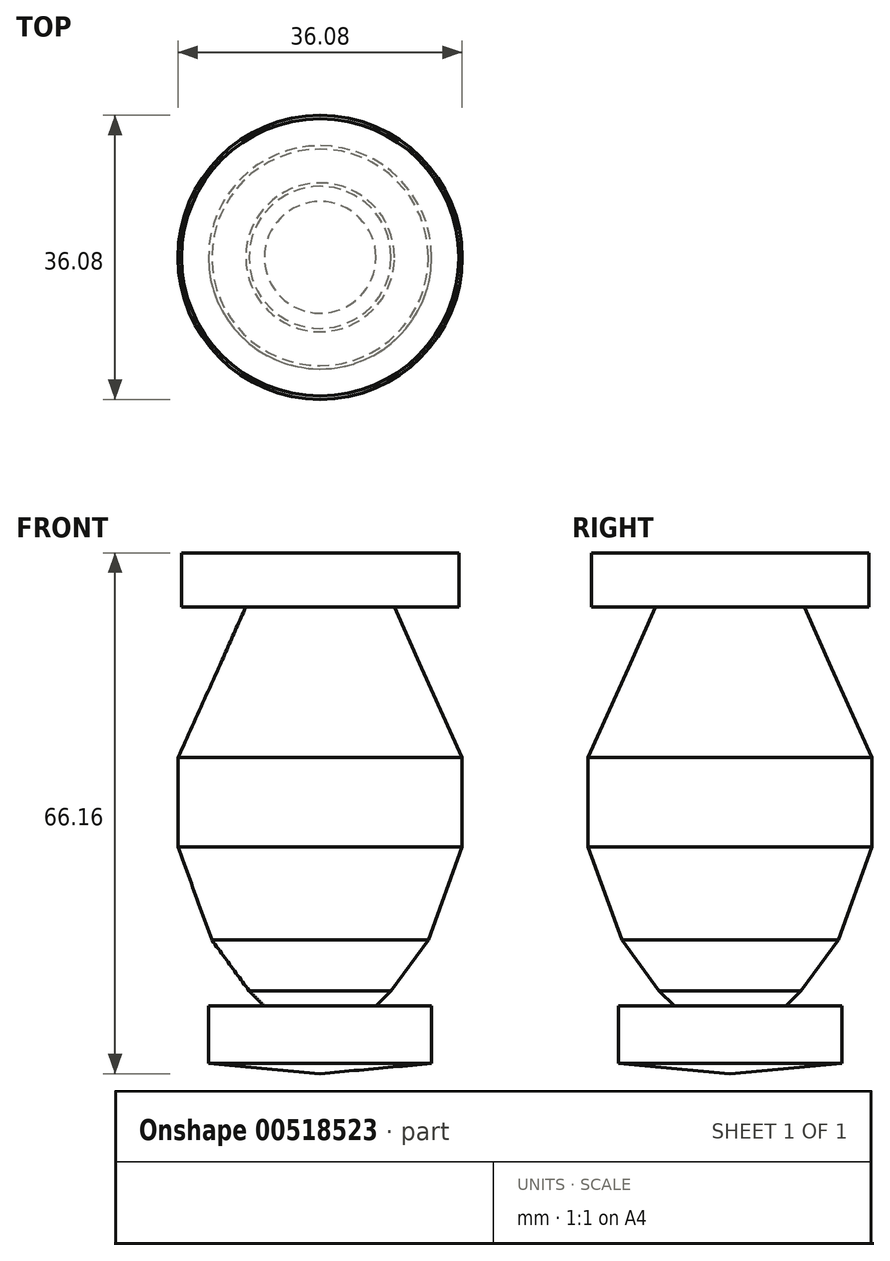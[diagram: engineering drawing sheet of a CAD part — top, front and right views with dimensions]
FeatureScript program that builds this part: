
annotation { "Feature Type Name" : "Feature", "Feature Type Description" : "" }
export const myFeature = defineFeature(function(context is Context, id is Id, definition is map)
    precondition{}
    {
        {
            var Q0;
            Q0=qCreatedBy(makeId("Front.planeOp"),FACE);
            var sketch = newSketch(context, id + "F0", { "sketchPlane" : qUnion([Q0])});
            skLineSegment(sketch, "E0", {"start": v(0, -31.04) * mm, "end": v(0, 35.12) * mm});
            skLineSegment(sketch, "E1", {"start": v(0, 35.12) * mm, "end": v(-17.61, 35.12) * mm});
            skLineSegment(sketch, "E2", {"start": v(-17.61, 35.12) * mm, "end": v(-17.61, 28.25) * mm});
            skLineSegment(sketch, "E3", {"start": v(-17.61, 28.25) * mm, "end": v(-9.45, 28.25) * mm});
            skLineSegment(sketch, "E4", {"start": v(-9.45, 28.25) * mm, "end": v(-12.89, 20.51) * mm});
            skLineSegment(sketch, "E5", {"start": v(-12.89, 20.51) * mm, "end": v(-18.04, 9.13) * mm});
            skLineSegment(sketch, "E6", {"start": v(-18.04, 9.13) * mm, "end": v(-18.04, -2.26) * mm});
            skLineSegment(sketch, "E7", {"start": v(-18.04, -2.26) * mm, "end": v(-13.75, -14.07) * mm});
            skLineSegment(sketch, "E8", {"start": v(-13.75, -14.07) * mm, "end": v(-9.02, -20.51) * mm});
            skLineSegment(sketch, "E9", {"start": v(-9.02, -20.51) * mm, "end": v(-7.09, -22.45) * mm});
            skLineSegment(sketch, "E10", {"start": v(-7.09, -22.45) * mm, "end": v(-14.18, -22.45) * mm});
            skLineSegment(sketch, "E11", {"start": v(-14.18, -22.45) * mm, "end": v(-14.18, -29.75) * mm});
            skLineSegment(sketch, "E12", {"start": v(-14.18, -29.75) * mm, "end": v(0, -31.04) * mm});
            skSolve(sketch);
        }
        {
            var Q0;
            Q0=makeQuery(id+"F0.imprint","IMPRINT",FACE,{"disambiguationData":[TD([[makeQuery(id+"F0.imprint","IMPRINT",EDGE,{"derivedFrom":sQuery(id+"F0.wireOp",EDGE,"E0")}),1.0]])]});
            var Q1;
            Q1=sQuery(id+"F0.wireOp",EDGE,"E0");
            revolve(context, id + "F1", {"entities" : qUnion([Q0]), "axis" : qUnion([Q1]), "revolveType" : RevolveType.FULL});
        }
    });
